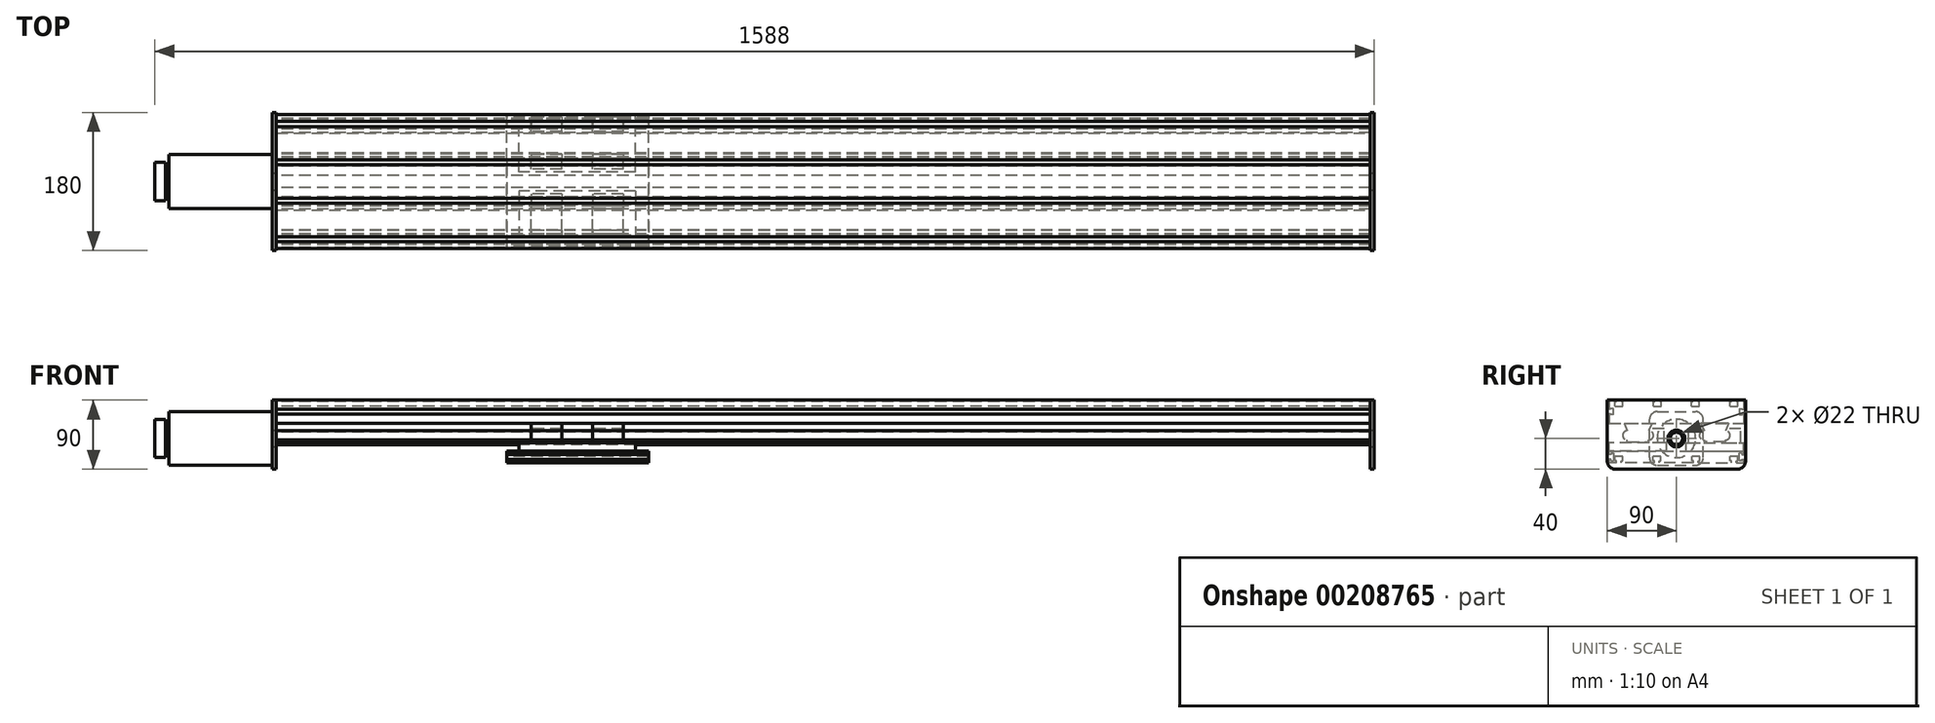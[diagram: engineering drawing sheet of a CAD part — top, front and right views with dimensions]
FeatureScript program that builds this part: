
annotation { "Feature Type Name" : "Feature", "Feature Type Description" : "" }
export const myFeature = defineFeature(function(context is Context, id is Id, definition is map)
    precondition{}
    {
        {
            var Q0;
            Q0=qCreatedBy(makeId("Right.planeOp"),FACE);
            var sketch = newSketch(context, id + "F0", { "sketchPlane" : qUnion([Q0])});
            skLineSegment(sketch, "E0", {"start": v(0, 0) * mm, "end": v(87.5, 0) * mm});
            skLineSegment(sketch, "E1", {"start": v(87.5, 0) * mm, "end": v(87.5, -30) * mm});
            skLineSegment(sketch, "E2.MirrorCS", {"start": v(0, 0) * mm, "end": v(-87.5, 0) * mm});
            skLineSegment(sketch, "E3.MirrorCS", {"start": v(-87.5, 0) * mm, "end": v(-87.5, -30) * mm});
            skLineSegment(sketch, "E4", {"start": v(87.5, 0) * mm, "end": v(78.2, 0) * mm});
            skLineSegment(sketch, "E5", {"start": v(78.2, 0) * mm, "end": v(78.2, -2) * mm});
            skLineSegment(sketch, "E6", {"start": v(78.2, 0) * mm, "end": v(71.75, 0) * mm});
            skLineSegment(sketch, "E7", {"start": v(71.75, 0) * mm, "end": v(71.75, -2) * mm});
            skLineSegment(sketch, "E8", {"start": v(74.98, -8) * mm, "end": v(79.98, -8) * mm});
            skLineSegment(sketch, "E9", {"start": v(74.98, -8) * mm, "end": v(69.98, -8) * mm});
            skLineSegment(sketch, "E10", {"start": v(69.98, -8) * mm, "end": v(69.98, -2) * mm});
            skLineSegment(sketch, "E11", {"start": v(69.98, -2) * mm, "end": v(71.75, -2) * mm});
            skLineSegment(sketch, "E12", {"start": v(74.98, 0) * mm, "end": v(74.98, -8) * mm, "construction": true});
            skLineSegment(sketch, "E13.MirrorCS", {"start": v(79.98, -8) * mm, "end": v(79.98, -2) * mm});
            skLineSegment(sketch, "E14.MirrorCS", {"start": v(79.98, -2) * mm, "end": v(78.2, -2) * mm});
            skLineSegment(sketch, "E15", {"start": v(87.5, 0) * mm, "end": v(28.2, 0) * mm});
            skLineSegment(sketch, "E16", {"start": v(28.2, 0) * mm, "end": v(28.2, -2) * mm});
            skLineSegment(sketch, "E17", {"start": v(28.2, 0) * mm, "end": v(21.75, 0) * mm});
            skLineSegment(sketch, "E18", {"start": v(24.98, 0) * mm, "end": v(24.98, -8) * mm, "construction": true});
            skLineSegment(sketch, "E19", {"start": v(24.98, -8) * mm, "end": v(29.98, -8) * mm});
            skLineSegment(sketch, "E20", {"start": v(24.98, -8) * mm, "end": v(19.98, -8) * mm});
            skLineSegment(sketch, "E21", {"start": v(29.98, -8) * mm, "end": v(29.98, -2) * mm});
            skLineSegment(sketch, "E22", {"start": v(29.98, -2) * mm, "end": v(28.2, -2) * mm});
            skLineSegment(sketch, "E23.MirrorCS", {"start": v(19.98, -8) * mm, "end": v(19.98, -2) * mm});
            skLineSegment(sketch, "E24.MirrorCS", {"start": v(19.98, -2) * mm, "end": v(21.75, -2) * mm});
            skLineSegment(sketch, "E25.MirrorCS", {"start": v(21.75, 0) * mm, "end": v(21.75, -2) * mm});
            skLineSegment(sketch, "E26", {"start": v(87.5, -30) * mm, "end": v(0, -30) * mm});
            skLineSegment(sketch, "E27.MirrorCS", {"start": v(-87.5, -30) * mm, "end": v(0, -30) * mm});
            skLineSegment(sketch, "E28", {"start": v(87.5, -15) * mm, "end": v(82, -15) * mm, "construction": true});
            skLineSegment(sketch, "E29", {"start": v(82, -15) * mm, "end": v(82, -11) * mm});
            skLineSegment(sketch, "E30", {"start": v(82, -15) * mm, "end": v(82, -19) * mm});
            skLineSegment(sketch, "E31", {"start": v(82, -11) * mm, "end": v(86, -11) * mm});
            skLineSegment(sketch, "E32", {"start": v(86, -11) * mm, "end": v(86, -12) * mm});
            skLineSegment(sketch, "E33", {"start": v(86, -12) * mm, "end": v(87.5, -12) * mm});
            skLineSegment(sketch, "E34.MirrorCS", {"start": v(82, -19) * mm, "end": v(86, -19) * mm});
            skLineSegment(sketch, "E35.MirrorCS", {"start": v(86, -19) * mm, "end": v(86, -18) * mm});
            skLineSegment(sketch, "E36.MirrorCS", {"start": v(86, -18) * mm, "end": v(87.5, -18) * mm});
            skLineSegment(sketch, "E37", {"start": v(87.5, -30) * mm, "end": v(68, -30) * mm});
            skLineSegment(sketch, "E38", {"start": v(87.5, -30) * mm, "end": v(87.5, -40) * mm, "construction": true});
            skLineSegment(sketch, "E39", {"start": v(87.5, -40) * mm, "end": v(64, -40) * mm, "construction": true});
            skLineSegment(sketch, "E40", {"start": v(68, -30) * mm, "end": v(64, -40) * mm});
            skLineSegment(sketch, "E41", {"start": v(0, 0) * mm, "end": v(0, -54.5) * mm, "construction": true});
            skLineSegment(sketch, "E42", {"start": v(0, -54.5) * mm, "end": v(87.5, -54.5) * mm, "construction": true});
            skLineSegment(sketch, "E43", {"start": v(64, -54.5) * mm, "end": v(64, -52) * mm});
            skLineSegment(sketch, "E44", {"start": v(64, -40) * mm, "end": v(64, -52) * mm, "construction": true});
            skArc(sketch, "E45", {"start": v(64, -52) * mm, "mid": v(70, -46) * mm, "end": v(64, -40) * mm});
            skLineSegment(sketch, "E46", {"start": v(64, -54.5) * mm, "end": v(36, -54.5) * mm});
            skLineSegment(sketch, "E47", {"start": v(50, -54.5) * mm, "end": v(50, -30) * mm, "construction": true});
            skLineSegment(sketch, "E48.MirrorCS", {"start": v(36, -54.5) * mm, "end": v(36, -52) * mm});
            skArc(sketch, "E49.MirrorCS", {"start": v(36, -52) * mm, "mid": v(30, -46) * mm, "end": v(36, -40) * mm});
            skLineSegment(sketch, "E50.MirrorCS", {"start": v(32, -30) * mm, "end": v(36, -40) * mm});
            skLineSegment(sketch, "E51.MirrorCS", {"start": v(-21.75, 0) * mm, "end": v(-21.75, -2) * mm});
            skLineSegment(sketch, "E52.MirrorCS", {"start": v(-19.98, -2) * mm, "end": v(-21.75, -2) * mm});
            skLineSegment(sketch, "E53.MirrorCS", {"start": v(-19.98, -8) * mm, "end": v(-19.98, -2) * mm});
            skLineSegment(sketch, "E54.MirrorCS", {"start": v(-24.98, -8) * mm, "end": v(-19.98, -8) * mm});
            skLineSegment(sketch, "E55.MirrorCS", {"start": v(-24.98, -8) * mm, "end": v(-29.98, -8) * mm});
            skLineSegment(sketch, "E56.MirrorCS", {"start": v(-29.98, -8) * mm, "end": v(-29.98, -2) * mm});
            skLineSegment(sketch, "E57.MirrorCS", {"start": v(-29.98, -2) * mm, "end": v(-28.2, -2) * mm});
            skLineSegment(sketch, "E58.MirrorCS", {"start": v(-28.2, 0) * mm, "end": v(-28.2, -2) * mm});
            skLineSegment(sketch, "E59.MirrorCS", {"start": v(-71.75, 0) * mm, "end": v(-71.75, -2) * mm});
            skLineSegment(sketch, "E60.MirrorCS", {"start": v(-69.98, -2) * mm, "end": v(-71.75, -2) * mm});
            skLineSegment(sketch, "E61.MirrorCS", {"start": v(-69.98, -8) * mm, "end": v(-69.98, -2) * mm});
            skLineSegment(sketch, "E62.MirrorCS", {"start": v(-74.98, -8) * mm, "end": v(-69.98, -8) * mm});
            skLineSegment(sketch, "E63.MirrorCS", {"start": v(-74.98, -8) * mm, "end": v(-79.98, -8) * mm});
            skLineSegment(sketch, "E64.MirrorCS", {"start": v(-79.98, -8) * mm, "end": v(-79.98, -2) * mm});
            skLineSegment(sketch, "E65.MirrorCS", {"start": v(-79.98, -2) * mm, "end": v(-78.2, -2) * mm});
            skLineSegment(sketch, "E66.MirrorCS", {"start": v(-78.2, 0) * mm, "end": v(-78.2, -2) * mm});
            skLineSegment(sketch, "E67.MirrorCS", {"start": v(-86, -12) * mm, "end": v(-87.5, -12) * mm});
            skLineSegment(sketch, "E68.MirrorCS", {"start": v(-86, -11) * mm, "end": v(-86, -12) * mm});
            skLineSegment(sketch, "E69.MirrorCS", {"start": v(-82, -11) * mm, "end": v(-86, -11) * mm});
            skLineSegment(sketch, "E70.MirrorCS", {"start": v(-82, -15) * mm, "end": v(-82, -11) * mm});
            skLineSegment(sketch, "E71.MirrorCS", {"start": v(-82, -15) * mm, "end": v(-82, -19) * mm});
            skLineSegment(sketch, "E72.MirrorCS", {"start": v(-82, -19) * mm, "end": v(-86, -19) * mm});
            skLineSegment(sketch, "E73.MirrorCS", {"start": v(-86, -19) * mm, "end": v(-86, -18) * mm});
            skLineSegment(sketch, "E74.MirrorCS", {"start": v(-86, -18) * mm, "end": v(-87.5, -18) * mm});
            skLineSegment(sketch, "E75.MirrorCS", {"start": v(-68, -30) * mm, "end": v(-64, -40) * mm});
            skArc(sketch, "E76.MirrorCS", {"start": v(-64, -52) * mm, "mid": v(-70, -46) * mm, "end": v(-64, -40) * mm});
            skLineSegment(sketch, "E77.MirrorCS", {"start": v(-64, -54.5) * mm, "end": v(-64, -52) * mm});
            skLineSegment(sketch, "E78.MirrorCS", {"start": v(-36, -54.5) * mm, "end": v(-36, -52) * mm});
            skArc(sketch, "E79.MirrorCS", {"start": v(-36, -52) * mm, "mid": v(-30, -46) * mm, "end": v(-36, -40) * mm});
            skLineSegment(sketch, "E80.MirrorCS", {"start": v(-32, -30) * mm, "end": v(-36, -40) * mm});
            skLineSegment(sketch, "E81", {"start": v(-64, -54.5) * mm, "end": v(-36, -54.5) * mm});
            skLineSegment(sketch, "E82", {"start": v(0, -54.5) * mm, "end": v(0, -55.5) * mm, "construction": true});
            skLineSegment(sketch, "E83", {"start": v(87.5, -54.5) * mm, "end": v(87.5, -55.5) * mm, "construction": true});
            skLineSegment(sketch, "E84", {"start": v(0, -81.5) * mm, "end": v(87.5, -81.5) * mm});
            skLineSegment(sketch, "E85", {"start": v(87.5, -81.5) * mm, "end": v(87.5, -55.5) * mm});
            skLineSegment(sketch, "E86", {"start": v(0, -55.5) * mm, "end": v(0, -81.5) * mm, "construction": true});
            skLineSegment(sketch, "E87", {"start": v(0, -55.5) * mm, "end": v(12.5, -55.5) * mm, "construction": true});
            skLineSegment(sketch, "E88", {"start": v(12.5, -66.5) * mm, "end": v(12.5, -55.5) * mm});
            skLineSegment(sketch, "E89", {"start": v(12.5, -66.5) * mm, "end": v(0, -66.5) * mm});
            skLineSegment(sketch, "E90", {"start": v(0, -66.5) * mm, "end": v(0, -81.5) * mm});
            skLineSegment(sketch, "E91.MirrorCS", {"start": v(0, -81.5) * mm, "end": v(-87.5, -81.5) * mm});
            skLineSegment(sketch, "E92.MirrorCS", {"start": v(-87.5, -81.5) * mm, "end": v(-87.5, -55.5) * mm});
            skLineSegment(sketch, "E93.MirrorCS", {"start": v(-12.5, -66.5) * mm, "end": v(0, -66.5) * mm});
            skLineSegment(sketch, "E94.MirrorCS", {"start": v(-12.5, -66.5) * mm, "end": v(-12.5, -55.5) * mm});
            skLineSegment(sketch, "E95", {"start": v(12.5, -55.5) * mm, "end": v(87.5, -55.5) * mm});
            skLineSegment(sketch, "E96.MirrorCS", {"start": v(-12.5, -55.5) * mm, "end": v(-87.5, -55.5) * mm});
            skLineSegment(sketch, "E97", {"start": v(-12.5, -66.5) * mm, "end": v(-87.5, -66.5) * mm});
            skLineSegment(sketch, "E98", {"start": v(12.5, -66.5) * mm, "end": v(87.5, -66.5) * mm});
            skLineSegment(sketch, "E99", {"start": v(-87.5, -55.5) * mm, "end": v(-84, -55.5) * mm, "construction": true});
            skLineSegment(sketch, "E100", {"start": v(-84, -55.5) * mm, "end": v(-84, -37.5) * mm});
            skLineSegment(sketch, "E101", {"start": v(-84, -37.5) * mm, "end": v(-65, -37.5) * mm});
            skLineSegment(sketch, "E102", {"start": v(-64, -54.5) * mm, "end": v(-64, -55.5) * mm});
            skLineSegment(sketch, "E103.MirrorCS", {"start": v(84, -37.5) * mm, "end": v(65, -37.5) * mm});
            skLineSegment(sketch, "E104.MirrorCS", {"start": v(84, -55.5) * mm, "end": v(84, -37.5) * mm});
            skLineSegment(sketch, "E105.MirrorCS", {"start": v(64, -54.5) * mm, "end": v(64, -55.5) * mm});
            skLineSegment(sketch, "E106", {"start": v(-50, -54.5) * mm, "end": v(-50, -30) * mm, "construction": true});
            skLineSegment(sketch, "E107.MirrorCS", {"start": v(-16, -37.5) * mm, "end": v(-35, -37.5) * mm});
            skLineSegment(sketch, "E108.MirrorCS", {"start": v(-16, -55.5) * mm, "end": v(-16, -37.5) * mm});
            skLineSegment(sketch, "E109.MirrorCS", {"start": v(-36, -54.5) * mm, "end": v(-36, -55.5) * mm});
            skLineSegment(sketch, "E110.MirrorCS", {"start": v(16, -37.5) * mm, "end": v(35, -37.5) * mm});
            skLineSegment(sketch, "E111.MirrorCS", {"start": v(16, -55.5) * mm, "end": v(16, -37.5) * mm});
            skLineSegment(sketch, "E112.MirrorCS", {"start": v(36, -54.5) * mm, "end": v(36, -55.5) * mm});
            skLineSegment(sketch, "E113", {"start": v(-87.5, -81.5) * mm, "end": v(-78.3, -81.5) * mm});
            skLineSegment(sketch, "E114", {"start": v(-78.3, -81.5) * mm, "end": v(-71.85, -81.5) * mm});
            skLineSegment(sketch, "E115", {"start": v(-71.85, -81.5) * mm, "end": v(-28.45, -81.5) * mm});
            skLineSegment(sketch, "E116", {"start": v(-28.45, -81.5) * mm, "end": v(-22, -81.5) * mm});
            skLineSegment(sketch, "E117", {"start": v(-22, -81.5) * mm, "end": v(0, -81.5) * mm});
            skLineSegment(sketch, "E118", {"start": v(-78.3, -81.5) * mm, "end": v(-78.3, -79) * mm});
            skLineSegment(sketch, "E119", {"start": v(-75.08, -81.5) * mm, "end": v(-75.08, -73.5) * mm, "construction": true});
            skLineSegment(sketch, "E120", {"start": v(-75.08, -73.5) * mm, "end": v(-80.08, -73.5) * mm});
            skLineSegment(sketch, "E121", {"start": v(-75.08, -73.5) * mm, "end": v(-70.08, -73.5) * mm});
            skLineSegment(sketch, "E122", {"start": v(-78.3, -79) * mm, "end": v(-80.08, -79) * mm});
            skLineSegment(sketch, "E123", {"start": v(-80.08, -79) * mm, "end": v(-80.08, -73.5) * mm});
            skLineSegment(sketch, "E124.MirrorCS", {"start": v(-70.08, -79) * mm, "end": v(-70.08, -73.5) * mm});
            skLineSegment(sketch, "E125.MirrorCS", {"start": v(-71.85, -79) * mm, "end": v(-70.08, -79) * mm});
            skLineSegment(sketch, "E126.MirrorCS", {"start": v(-71.85, -81.5) * mm, "end": v(-71.85, -79) * mm});
            skLineSegment(sketch, "E127", {"start": v(-50.15, -81.5) * mm, "end": v(-50.15, -66.5) * mm, "construction": true});
            skLineSegment(sketch, "E128.MirrorCS", {"start": v(-28.45, -81.5) * mm, "end": v(-28.45, -79) * mm});
            skLineSegment(sketch, "E129.MirrorCS", {"start": v(-28.45, -79) * mm, "end": v(-30.23, -79) * mm});
            skLineSegment(sketch, "E130.MirrorCS", {"start": v(-30.23, -79) * mm, "end": v(-30.23, -73.5) * mm});
            skLineSegment(sketch, "E131.MirrorCS", {"start": v(-25.22, -73.5) * mm, "end": v(-30.23, -73.5) * mm});
            skLineSegment(sketch, "E132.MirrorCS", {"start": v(-25.22, -73.5) * mm, "end": v(-20.22, -73.5) * mm});
            skLineSegment(sketch, "E133.MirrorCS", {"start": v(-20.22, -79) * mm, "end": v(-20.22, -73.5) * mm});
            skLineSegment(sketch, "E134.MirrorCS", {"start": v(-22, -79) * mm, "end": v(-20.22, -79) * mm});
            skLineSegment(sketch, "E135.MirrorCS", {"start": v(-22, -81.5) * mm, "end": v(-22, -79) * mm});
            skLineSegment(sketch, "E136.MirrorCS", {"start": v(22, -81.5) * mm, "end": v(22, -79) * mm});
            skLineSegment(sketch, "E137.MirrorCS", {"start": v(22, -79) * mm, "end": v(20.23, -79) * mm});
            skLineSegment(sketch, "E138.MirrorCS", {"start": v(20.23, -79) * mm, "end": v(20.23, -73.5) * mm});
            skLineSegment(sketch, "E139.MirrorCS", {"start": v(25.23, -73.5) * mm, "end": v(20.23, -73.5) * mm});
            skLineSegment(sketch, "E140.MirrorCS", {"start": v(25.23, -73.5) * mm, "end": v(30.23, -73.5) * mm});
            skLineSegment(sketch, "E141.MirrorCS", {"start": v(30.23, -79) * mm, "end": v(30.23, -73.5) * mm});
            skLineSegment(sketch, "E142.MirrorCS", {"start": v(28.45, -79) * mm, "end": v(30.23, -79) * mm});
            skLineSegment(sketch, "E143.MirrorCS", {"start": v(28.45, -81.5) * mm, "end": v(28.45, -79) * mm});
            skLineSegment(sketch, "E144.MirrorCS", {"start": v(71.85, -81.5) * mm, "end": v(71.85, -79) * mm});
            skLineSegment(sketch, "E145.MirrorCS", {"start": v(71.85, -79) * mm, "end": v(70.08, -79) * mm});
            skLineSegment(sketch, "E146.MirrorCS", {"start": v(70.08, -79) * mm, "end": v(70.08, -73.5) * mm});
            skLineSegment(sketch, "E147.MirrorCS", {"start": v(75.08, -73.5) * mm, "end": v(70.08, -73.5) * mm});
            skLineSegment(sketch, "E148.MirrorCS", {"start": v(75.08, -73.5) * mm, "end": v(80.08, -73.5) * mm});
            skLineSegment(sketch, "E149.MirrorCS", {"start": v(80.08, -79) * mm, "end": v(80.08, -73.5) * mm});
            skLineSegment(sketch, "E150.MirrorCS", {"start": v(78.3, -79) * mm, "end": v(80.08, -79) * mm});
            skLineSegment(sketch, "E151.MirrorCS", {"start": v(78.3, -81.5) * mm, "end": v(78.3, -79) * mm});
            skLineSegment(sketch, "E152", {"start": v(-82.08, -69) * mm, "end": v(-82.08, -79) * mm});
            skLineSegment(sketch, "E153", {"start": v(-87.5, -79) * mm, "end": v(-85, -79) * mm, "construction": true});
            skLineSegment(sketch, "E154", {"start": v(-85, -79) * mm, "end": v(-82.08, -79) * mm});
            skLineSegment(sketch, "E155", {"start": v(-85, -79) * mm, "end": v(-85, -77) * mm});
            skLineSegment(sketch, "E156", {"start": v(-85, -77) * mm, "end": v(-87.5, -77) * mm});
            skLineSegment(sketch, "E157", {"start": v(-82.08, -74) * mm, "end": v(-87.5, -74) * mm, "construction": true});
            skLineSegment(sketch, "E158.MirrorCS", {"start": v(-85, -71) * mm, "end": v(-87.5, -71) * mm});
            skLineSegment(sketch, "E159.MirrorCS", {"start": v(-85, -69) * mm, "end": v(-85, -71) * mm});
            skLineSegment(sketch, "E160.MirrorCS", {"start": v(-85, -69) * mm, "end": v(-82.08, -69) * mm});
            skLineSegment(sketch, "E161.MirrorCS", {"start": v(-82.08, -79) * mm, "end": v(-82.08, -69) * mm});
            skLineSegment(sketch, "E162", {"start": v(-87.5, -66.5) * mm, "end": v(-87.5, -74) * mm, "construction": true});
            skLineSegment(sketch, "E163.MirrorCS", {"start": v(85, -77) * mm, "end": v(87.5, -77) * mm});
            skLineSegment(sketch, "E164.MirrorCS", {"start": v(85, -79) * mm, "end": v(85, -77) * mm});
            skLineSegment(sketch, "E165.MirrorCS", {"start": v(85, -79) * mm, "end": v(82.08, -79) * mm});
            skLineSegment(sketch, "E166.MirrorCS", {"start": v(82.08, -79) * mm, "end": v(82.08, -69) * mm});
            skLineSegment(sketch, "E167.MirrorCS", {"start": v(85, -69) * mm, "end": v(82.08, -69) * mm});
            skLineSegment(sketch, "E168.MirrorCS", {"start": v(85, -69) * mm, "end": v(85, -71) * mm});
            skLineSegment(sketch, "E169.MirrorCS", {"start": v(85, -71) * mm, "end": v(87.5, -71) * mm});
            skSolve(sketch);
        }
        {
            var Q0;
            {var subQ22=sQuery(id+"F0.wireOp",EDGE,"E0");Q0=makeQuery(id+"F0.imprint","IMPRINT",FACE,{"disambiguationData":[TD([[makeQuery(id+"F0.imprint","IMPRINT",EDGE,{"derivedFrom":subQ22}),-1.0]])]});}
            extrude(context, id + "F1", {"entities" : qUnion([Q0]), "depth" : 1425 * mm});
        }
        {
            var Q0;
            {var subQ0=sQuery(id+"F0.wireOp",EDGE,"E40");Q0=makeQuery(id+"F0.imprint","IMPRINT",FACE,{"disambiguationData":[TD([[makeQuery(id+"F0.imprint","IMPRINT",EDGE,{"derivedFrom":subQ0}),-1.0]])]});}
            var Q1;
            {var subQ0=sQuery(id+"F0.wireOp",EDGE,"E75.MirrorCS");Q1=makeQuery(id+"F0.imprint","IMPRINT",FACE,{"disambiguationData":[TD([[makeQuery(id+"F0.imprint","IMPRINT",EDGE,{"derivedFrom":subQ0}),1.0]])]});}
            extrude(context, id + "F2", {"entities" : qUnion([Q0, Q1]), "depth" : 1425 * mm});
        }
        {
            var Q0;
            Q0=makeQuery(id+"F2.opExtrude","SWEPT_EDGE",EDGE,{"disambiguationData":[OSD([sQuery(id+"F0.wireOp",EDGE,"E77.MirrorCS"),sQuery(id+"F0.wireOp",EDGE,"E81")])]});
            var Q1;
            Q1=makeQuery(id+"F2.opExtrude","SWEPT_EDGE",EDGE,{"disambiguationData":[OSD([sQuery(id+"F0.wireOp",EDGE,"E78.MirrorCS"),sQuery(id+"F0.wireOp",EDGE,"E81")])]});
            var Q2;
            Q2=makeQuery(id+"F2.opExtrude","SWEPT_EDGE",EDGE,{"disambiguationData":[OSD([sQuery(id+"F0.wireOp",EDGE,"E46"),sQuery(id+"F0.wireOp",EDGE,"E48.MirrorCS")])]});
            var Q3;
            Q3=makeQuery(id+"F2.opExtrude","SWEPT_EDGE",EDGE,{"disambiguationData":[OSD([sQuery(id+"F0.wireOp",EDGE,"E43"),sQuery(id+"F0.wireOp",EDGE,"E46")])]});
            chamfer(context, id + "F3", {"entities" : qUnion([Q0, Q1, Q2, Q3]), "width" : 1 * mm, "tangentPropagation" : true});
        }
        {
            var Q0;
            Q0=makeQuery(id+"F0.imprint","IMPRINT",FACE,{"disambiguationData":[TD([[makeQuery(id+"F0.imprint","IMPRINT",EDGE,{"derivedFrom":sQuery(id+"F0.wireOp",EDGE,"E94.MirrorCS")}),1.0]])]});
            var Q1;
            Q1=makeQuery(id+"F0.imprint","IMPRINT",FACE,{"disambiguationData":[TD([[makeQuery(id+"F0.imprint","IMPRINT",EDGE,{"derivedFrom":sQuery(id+"F0.wireOp",EDGE,"E88")}),-1.0]])]});
            extrude(context, id + "F4", {"entities" : qUnion([Q0, Q1]), "depth" : 152 * mm});
        }
        {
            var Q0;
            Q0=makeQuery(id+"F0.imprint","IMPRINT",FACE,{"disambiguationData":[TD([[makeQuery(id+"F0.imprint","IMPRINT",EDGE,{"derivedFrom":sQuery(id+"F0.wireOp",EDGE,"E90")}),-1.0]])]});
            var Q1;
            {var subQ1=sQuery(id+"F0.wireOp",EDGE,"E84");Q1=makeQuery(id+"F0.imprint","IMPRINT",FACE,{"disambiguationData":[TD([[makeQuery(id+"F0.imprint","IMPRINT",EDGE,{"derivedFrom":subQ1}),1.0]])]});}
            extrude(context, id + "F5", {"entities" : qUnion([Q0, Q1]), "depth" : 185 * mm});
        }
        {
            var Q0;
            {var subQ4=sQuery(id+"F0.wireOp",EDGE,"E76.MirrorCS");Q0=makeQuery(id+"F0.imprint","IMPRINT",FACE,{"disambiguationData":[TD([[makeQuery(id+"F0.imprint","IMPRINT",EDGE,{"derivedFrom":subQ4}),1.0]])]});}
            var Q1;
            Q1=makeQuery(id+"F0.imprint","IMPRINT",FACE,{"disambiguationData":[TD([[makeQuery(id+"F0.imprint","IMPRINT",EDGE,{"derivedFrom":sQuery(id+"F0.wireOp",EDGE,"E43")}),-1.0]])]});
            var Q2;
            Q2=makeQuery(id+"F0.imprint","IMPRINT",FACE,{"disambiguationData":[TD([[makeQuery(id+"F0.imprint","IMPRINT",EDGE,{"derivedFrom":sQuery(id+"F0.wireOp",EDGE,"E78.MirrorCS")}),-1.0]])]});
            var Q3;
            Q3=makeQuery(id+"F0.imprint","IMPRINT",FACE,{"disambiguationData":[TD([[makeQuery(id+"F0.imprint","IMPRINT",EDGE,{"derivedFrom":sQuery(id+"F0.wireOp",EDGE,"E48.MirrorCS")}),1.0]])]});
            extrude(context, id + "F6", {"entities" : qUnion([Q0, Q1, Q2, Q3]), "depth" : 40 * mm});
        }
        {
            var Q0;
            Q0=makeQuery(id+"F4.opExtrude","SWEPT_BODY",BODY,{"disambiguationData":[OSD([sQuery(id+"F0.wireOp",EDGE,"E85"),sQuery(id+"F0.wireOp",EDGE,"E88"),sQuery(id+"F0.wireOp",EDGE,"E95"),sQuery(id+"F0.wireOp",EDGE,"E98")])]});
            var Q1;
            Q1=makeQuery(id+"F4.opExtrude","SWEPT_BODY",BODY,{"disambiguationData":[OSD([sQuery(id+"F0.wireOp",EDGE,"E92.MirrorCS"),sQuery(id+"F0.wireOp",EDGE,"E94.MirrorCS"),sQuery(id+"F0.wireOp",EDGE,"E96.MirrorCS"),sQuery(id+"F0.wireOp",EDGE,"E97")])]});
            transform(context, id + "F7", {"entities" : qUnion([Q0, Q1]), "transformType" : TransformType.TRANSLATION_3D, "dx" : 16 * mm, "dy" : 0 * mm, "dz" : 0 * mm, "makeCopy" : false});
        }
        {
            var Q0;
            Q0=makeQuery(id+"F6.opExtrude","SWEPT_BODY",BODY,{"disambiguationData":[OSD([sQuery(id+"F0.wireOp",EDGE,"E75.MirrorCS"),sQuery(id+"F0.wireOp",EDGE,"E76.MirrorCS"),sQuery(id+"F0.wireOp",EDGE,"E77.MirrorCS"),sQuery(id+"F0.wireOp",EDGE,"E96.MirrorCS"),sQuery(id+"F0.wireOp",EDGE,"E100"),sQuery(id+"F0.wireOp",EDGE,"E101"),sQuery(id+"F0.wireOp",EDGE,"E102")])]});
            var Q1;
            Q1=makeQuery(id+"F6.opExtrude","SWEPT_BODY",BODY,{"disambiguationData":[OSD([sQuery(id+"F0.wireOp",EDGE,"E78.MirrorCS"),sQuery(id+"F0.wireOp",EDGE,"E79.MirrorCS"),sQuery(id+"F0.wireOp",EDGE,"E80.MirrorCS"),sQuery(id+"F0.wireOp",EDGE,"E96.MirrorCS"),sQuery(id+"F0.wireOp",EDGE,"E107.MirrorCS"),sQuery(id+"F0.wireOp",EDGE,"E108.MirrorCS"),sQuery(id+"F0.wireOp",EDGE,"E109.MirrorCS")])]});
            var Q2;
            Q2=makeQuery(id+"F6.opExtrude","SWEPT_BODY",BODY,{"disambiguationData":[OSD([sQuery(id+"F0.wireOp",EDGE,"E48.MirrorCS"),sQuery(id+"F0.wireOp",EDGE,"E49.MirrorCS"),sQuery(id+"F0.wireOp",EDGE,"E50.MirrorCS"),sQuery(id+"F0.wireOp",EDGE,"E95"),sQuery(id+"F0.wireOp",EDGE,"E110.MirrorCS"),sQuery(id+"F0.wireOp",EDGE,"E111.MirrorCS"),sQuery(id+"F0.wireOp",EDGE,"E112.MirrorCS")])]});
            var Q3;
            Q3=makeQuery(id+"F6.opExtrude","SWEPT_BODY",BODY,{"disambiguationData":[OSD([sQuery(id+"F0.wireOp",EDGE,"E40"),sQuery(id+"F0.wireOp",EDGE,"E43"),sQuery(id+"F0.wireOp",EDGE,"E45"),sQuery(id+"F0.wireOp",EDGE,"E95"),sQuery(id+"F0.wireOp",EDGE,"E103.MirrorCS"),sQuery(id+"F0.wireOp",EDGE,"E104.MirrorCS"),sQuery(id+"F0.wireOp",EDGE,"E105.MirrorCS")])]});
            transform(context, id + "F8", {"entities" : qUnion([Q0, Q1, Q2, Q3]), "transformType" : TransformType.TRANSLATION_3D, "dx" : 32 * mm, "dy" : 0 * mm, "dz" : 0 * mm, "makeCopy" : false});
        }
        {
            var Q0;
            Q0=makeQuery(id+"F6.opExtrude","SWEPT_BODY",BODY,{"disambiguationData":[OSD([sQuery(id+"F0.wireOp",EDGE,"E75.MirrorCS"),sQuery(id+"F0.wireOp",EDGE,"E76.MirrorCS"),sQuery(id+"F0.wireOp",EDGE,"E77.MirrorCS"),sQuery(id+"F0.wireOp",EDGE,"E96.MirrorCS"),sQuery(id+"F0.wireOp",EDGE,"E100"),sQuery(id+"F0.wireOp",EDGE,"E101"),sQuery(id+"F0.wireOp",EDGE,"E102")])]});
            var Q1;
            Q1=makeQuery(id+"F6.opExtrude","SWEPT_BODY",BODY,{"disambiguationData":[OSD([sQuery(id+"F0.wireOp",EDGE,"E78.MirrorCS"),sQuery(id+"F0.wireOp",EDGE,"E79.MirrorCS"),sQuery(id+"F0.wireOp",EDGE,"E80.MirrorCS"),sQuery(id+"F0.wireOp",EDGE,"E96.MirrorCS"),sQuery(id+"F0.wireOp",EDGE,"E107.MirrorCS"),sQuery(id+"F0.wireOp",EDGE,"E108.MirrorCS"),sQuery(id+"F0.wireOp",EDGE,"E109.MirrorCS")])]});
            var Q2;
            Q2=makeQuery(id+"F6.opExtrude","SWEPT_BODY",BODY,{"disambiguationData":[OSD([sQuery(id+"F0.wireOp",EDGE,"E48.MirrorCS"),sQuery(id+"F0.wireOp",EDGE,"E49.MirrorCS"),sQuery(id+"F0.wireOp",EDGE,"E50.MirrorCS"),sQuery(id+"F0.wireOp",EDGE,"E95"),sQuery(id+"F0.wireOp",EDGE,"E110.MirrorCS"),sQuery(id+"F0.wireOp",EDGE,"E111.MirrorCS"),sQuery(id+"F0.wireOp",EDGE,"E112.MirrorCS")])]});
            var Q3;
            Q3=makeQuery(id+"F6.opExtrude","SWEPT_BODY",BODY,{"disambiguationData":[OSD([sQuery(id+"F0.wireOp",EDGE,"E40"),sQuery(id+"F0.wireOp",EDGE,"E43"),sQuery(id+"F0.wireOp",EDGE,"E45"),sQuery(id+"F0.wireOp",EDGE,"E95"),sQuery(id+"F0.wireOp",EDGE,"E103.MirrorCS"),sQuery(id+"F0.wireOp",EDGE,"E104.MirrorCS"),sQuery(id+"F0.wireOp",EDGE,"E105.MirrorCS")])]});
            transform(context, id + "F9", {"entities" : qUnion([Q0, Q1, Q2, Q3]), "transformType" : TransformType.TRANSLATION_3D, "dx" : 80 * mm, "dy" : 0 * mm, "dz" : 0 * mm, "makeCopy" : true});
        }
        {
            var Q0;
            Q0=makeQuery(id+"F5.opExtrude","SWEPT_BODY",BODY,{"disambiguationData":[OSD([sQuery(id+"F0.wireOp",EDGE,"E84"),sQuery(id+"F0.wireOp",EDGE,"E85"),sQuery(id+"F0.wireOp",EDGE,"E89"),sQuery(id+"F0.wireOp",EDGE,"E92.MirrorCS"),sQuery(id+"F0.wireOp",EDGE,"E93.MirrorCS"),sQuery(id+"F0.wireOp",EDGE,"E97"),sQuery(id+"F0.wireOp",EDGE,"E98"),sQuery(id+"F0.wireOp",EDGE,"E113"),sQuery(id+"F0.wireOp",EDGE,"E115"),sQuery(id+"F0.wireOp",EDGE,"E117"),sQuery(id+"F0.wireOp",EDGE,"E118"),sQuery(id+"F0.wireOp",EDGE,"E120"),sQuery(id+"F0.wireOp",EDGE,"E121"),sQuery(id+"F0.wireOp",EDGE,"E122"),sQuery(id+"F0.wireOp",EDGE,"E123"),sQuery(id+"F0.wireOp",EDGE,"E124.MirrorCS"),sQuery(id+"F0.wireOp",EDGE,"E125.MirrorCS"),sQuery(id+"F0.wireOp",EDGE,"E126.MirrorCS"),sQuery(id+"F0.wireOp",EDGE,"E128.MirrorCS"),sQuery(id+"F0.wireOp",EDGE,"E129.MirrorCS"),sQuery(id+"F0.wireOp",EDGE,"E130.MirrorCS"),sQuery(id+"F0.wireOp",EDGE,"E131.MirrorCS"),sQuery(id+"F0.wireOp",EDGE,"E132.MirrorCS"),sQuery(id+"F0.wireOp",EDGE,"E133.MirrorCS"),sQuery(id+"F0.wireOp",EDGE,"E134.MirrorCS"),sQuery(id+"F0.wireOp",EDGE,"E135.MirrorCS"),sQuery(id+"F0.wireOp",EDGE,"E136.MirrorCS"),sQuery(id+"F0.wireOp",EDGE,"E137.MirrorCS"),sQuery(id+"F0.wireOp",EDGE,"E138.MirrorCS"),sQuery(id+"F0.wireOp",EDGE,"E139.MirrorCS"),sQuery(id+"F0.wireOp",EDGE,"E140.MirrorCS"),sQuery(id+"F0.wireOp",EDGE,"E141.MirrorCS"),sQuery(id+"F0.wireOp",EDGE,"E142.MirrorCS"),sQuery(id+"F0.wireOp",EDGE,"E143.MirrorCS"),sQuery(id+"F0.wireOp",EDGE,"E144.MirrorCS"),sQuery(id+"F0.wireOp",EDGE,"E145.MirrorCS"),sQuery(id+"F0.wireOp",EDGE,"E146.MirrorCS"),sQuery(id+"F0.wireOp",EDGE,"E147.MirrorCS"),sQuery(id+"F0.wireOp",EDGE,"E148.MirrorCS"),sQuery(id+"F0.wireOp",EDGE,"E149.MirrorCS"),sQuery(id+"F0.wireOp",EDGE,"E150.MirrorCS"),sQuery(id+"F0.wireOp",EDGE,"E151.MirrorCS"),sQuery(id+"F0.wireOp",EDGE,"E154"),sQuery(id+"F0.wireOp",EDGE,"E155"),sQuery(id+"F0.wireOp",EDGE,"E156"),sQuery(id+"F0.wireOp",EDGE,"E158.MirrorCS"),sQuery(id+"F0.wireOp",EDGE,"E159.MirrorCS"),sQuery(id+"F0.wireOp",EDGE,"E160.MirrorCS"),sQuery(id+"F0.wireOp",EDGE,"E161.MirrorCS"),sQuery(id+"F0.wireOp",EDGE,"E163.MirrorCS"),sQuery(id+"F0.wireOp",EDGE,"E164.MirrorCS"),sQuery(id+"F0.wireOp",EDGE,"E165.MirrorCS"),sQuery(id+"F0.wireOp",EDGE,"E166.MirrorCS"),sQuery(id+"F0.wireOp",EDGE,"E167.MirrorCS"),sQuery(id+"F0.wireOp",EDGE,"E168.MirrorCS"),sQuery(id+"F0.wireOp",EDGE,"E169.MirrorCS")])]});
            var Q1;
            Q1=makeQuery(id+"F4.opExtrude","SWEPT_BODY",BODY,{"disambiguationData":[OSD([sQuery(id+"F0.wireOp",EDGE,"E92.MirrorCS"),sQuery(id+"F0.wireOp",EDGE,"E94.MirrorCS"),sQuery(id+"F0.wireOp",EDGE,"E96.MirrorCS"),sQuery(id+"F0.wireOp",EDGE,"E97")])]});
            var Q2;
            Q2=makeQuery(id+"F4.opExtrude","SWEPT_BODY",BODY,{"disambiguationData":[OSD([sQuery(id+"F0.wireOp",EDGE,"E85"),sQuery(id+"F0.wireOp",EDGE,"E88"),sQuery(id+"F0.wireOp",EDGE,"E95"),sQuery(id+"F0.wireOp",EDGE,"E98")])]});
            var Q3;
            Q3=makeQuery(id+"F9.opPattern","COPY",BODY,{"derivedFrom":makeQuery(id+"F6.opExtrude","SWEPT_BODY",BODY,{"disambiguationData":[OSD([sQuery(id+"F0.wireOp",EDGE,"E75.MirrorCS"),sQuery(id+"F0.wireOp",EDGE,"E76.MirrorCS"),sQuery(id+"F0.wireOp",EDGE,"E77.MirrorCS"),sQuery(id+"F0.wireOp",EDGE,"E96.MirrorCS"),sQuery(id+"F0.wireOp",EDGE,"E100"),sQuery(id+"F0.wireOp",EDGE,"E101"),sQuery(id+"F0.wireOp",EDGE,"E102")])]}),"instanceName":"1"});
            var Q4;
            Q4=makeQuery(id+"F6.opExtrude","SWEPT_BODY",BODY,{"disambiguationData":[OSD([sQuery(id+"F0.wireOp",EDGE,"E75.MirrorCS"),sQuery(id+"F0.wireOp",EDGE,"E76.MirrorCS"),sQuery(id+"F0.wireOp",EDGE,"E77.MirrorCS"),sQuery(id+"F0.wireOp",EDGE,"E96.MirrorCS"),sQuery(id+"F0.wireOp",EDGE,"E100"),sQuery(id+"F0.wireOp",EDGE,"E101"),sQuery(id+"F0.wireOp",EDGE,"E102")])]});
            var Q5;
            Q5=makeQuery(id+"F9.opPattern","COPY",BODY,{"derivedFrom":makeQuery(id+"F6.opExtrude","SWEPT_BODY",BODY,{"disambiguationData":[OSD([sQuery(id+"F0.wireOp",EDGE,"E40"),sQuery(id+"F0.wireOp",EDGE,"E43"),sQuery(id+"F0.wireOp",EDGE,"E45"),sQuery(id+"F0.wireOp",EDGE,"E95"),sQuery(id+"F0.wireOp",EDGE,"E103.MirrorCS"),sQuery(id+"F0.wireOp",EDGE,"E104.MirrorCS"),sQuery(id+"F0.wireOp",EDGE,"E105.MirrorCS")])]}),"instanceName":"1"});
            var Q6;
            Q6=makeQuery(id+"F6.opExtrude","SWEPT_BODY",BODY,{"disambiguationData":[OSD([sQuery(id+"F0.wireOp",EDGE,"E40"),sQuery(id+"F0.wireOp",EDGE,"E43"),sQuery(id+"F0.wireOp",EDGE,"E45"),sQuery(id+"F0.wireOp",EDGE,"E95"),sQuery(id+"F0.wireOp",EDGE,"E103.MirrorCS"),sQuery(id+"F0.wireOp",EDGE,"E104.MirrorCS"),sQuery(id+"F0.wireOp",EDGE,"E105.MirrorCS")])]});
            var Q7;
            Q7=makeQuery(id+"F6.opExtrude","SWEPT_BODY",BODY,{"disambiguationData":[OSD([sQuery(id+"F0.wireOp",EDGE,"E48.MirrorCS"),sQuery(id+"F0.wireOp",EDGE,"E49.MirrorCS"),sQuery(id+"F0.wireOp",EDGE,"E50.MirrorCS"),sQuery(id+"F0.wireOp",EDGE,"E95"),sQuery(id+"F0.wireOp",EDGE,"E110.MirrorCS"),sQuery(id+"F0.wireOp",EDGE,"E111.MirrorCS"),sQuery(id+"F0.wireOp",EDGE,"E112.MirrorCS")])]});
            var Q8;
            Q8=makeQuery(id+"F9.opPattern","COPY",BODY,{"derivedFrom":makeQuery(id+"F6.opExtrude","SWEPT_BODY",BODY,{"disambiguationData":[OSD([sQuery(id+"F0.wireOp",EDGE,"E48.MirrorCS"),sQuery(id+"F0.wireOp",EDGE,"E49.MirrorCS"),sQuery(id+"F0.wireOp",EDGE,"E50.MirrorCS"),sQuery(id+"F0.wireOp",EDGE,"E95"),sQuery(id+"F0.wireOp",EDGE,"E110.MirrorCS"),sQuery(id+"F0.wireOp",EDGE,"E111.MirrorCS"),sQuery(id+"F0.wireOp",EDGE,"E112.MirrorCS")])]}),"instanceName":"1"});
            var Q9;
            Q9=makeQuery(id+"F6.opExtrude","SWEPT_BODY",BODY,{"disambiguationData":[OSD([sQuery(id+"F0.wireOp",EDGE,"E78.MirrorCS"),sQuery(id+"F0.wireOp",EDGE,"E79.MirrorCS"),sQuery(id+"F0.wireOp",EDGE,"E80.MirrorCS"),sQuery(id+"F0.wireOp",EDGE,"E96.MirrorCS"),sQuery(id+"F0.wireOp",EDGE,"E107.MirrorCS"),sQuery(id+"F0.wireOp",EDGE,"E108.MirrorCS"),sQuery(id+"F0.wireOp",EDGE,"E109.MirrorCS")])]});
            var Q10;
            Q10=makeQuery(id+"F9.opPattern","COPY",BODY,{"derivedFrom":makeQuery(id+"F6.opExtrude","SWEPT_BODY",BODY,{"disambiguationData":[OSD([sQuery(id+"F0.wireOp",EDGE,"E78.MirrorCS"),sQuery(id+"F0.wireOp",EDGE,"E79.MirrorCS"),sQuery(id+"F0.wireOp",EDGE,"E80.MirrorCS"),sQuery(id+"F0.wireOp",EDGE,"E96.MirrorCS"),sQuery(id+"F0.wireOp",EDGE,"E107.MirrorCS"),sQuery(id+"F0.wireOp",EDGE,"E108.MirrorCS"),sQuery(id+"F0.wireOp",EDGE,"E109.MirrorCS")])]}),"instanceName":"1"});
            transform(context, id + "F10", {"entities" : qUnion([Q0, Q1, Q2, Q3, Q4, Q5, Q6, Q7, Q8, Q9, Q10]), "transformType" : TransformType.TRANSLATION_3D, "dx" : 300 * mm, "dy" : 0 * mm, "dz" : 0 * mm, "makeCopy" : false});
        }
        {
            var Q0;
            Q0=qCreatedBy(makeId("Right.planeOp"),FACE);
            var sketch = newSketch(context, id + "F11", { "sketchPlane" : qUnion([Q0])});
            skLineSegment(sketch, "E170", {"start": v(0, 0) * mm, "end": v(-90, 0) * mm});
            skLineSegment(sketch, "E171", {"start": v(0, 0) * mm, "end": v(90, 0) * mm});
            skLineSegment(sketch, "E172", {"start": v(-90, 0) * mm, "end": v(-90, -90) * mm});
            skLineSegment(sketch, "E173", {"start": v(-90, -90) * mm, "end": v(90, -90) * mm});
            skLineSegment(sketch, "E174", {"start": v(90, -90) * mm, "end": v(90, 0) * mm});
            skLineSegment(sketch, "E175", {"start": v(0, 0) * mm, "end": v(0, -50) * mm, "construction": true});
            skCircle(sketch, "E176", {"center": v(0, -50) * mm, "radius": 11 * mm});
            skCircle(sketch, "E177", {"center": v(0, -50) * mm, "radius": 8 * mm});
            skSolve(sketch);
        }
        {
            var Q0;
            Q0=makeQuery(id+"F11.imprint","IMPRINT",FACE,{"disambiguationData":[TD([[makeQuery(id+"F11.imprint","IMPRINT",EDGE,{"derivedFrom":sQuery(id+"F11.wireOp",EDGE,"E170")}),1.0]])]});
            extrude(context, id + "F12", {"entities" : qUnion([Q0]), "oppositeDirection" : true, "depth" : 5 * mm});
        }
        {
            var Q0;
            Q0=makeQuery(id+"F12.opExtrude","SWEPT_EDGE",EDGE,{"disambiguationData":[OSD([sQuery(id+"F11.wireOp",EDGE,"E172"),sQuery(id+"F11.wireOp",EDGE,"E173")])]});
            var Q1;
            Q1=makeQuery(id+"F12.opExtrude","SWEPT_EDGE",EDGE,{"disambiguationData":[OSD([sQuery(id+"F11.wireOp",EDGE,"E173"),sQuery(id+"F11.wireOp",EDGE,"E174")])]});
            fillet(context, id + "F13", {"entities" : qUnion([Q0, Q1]), "radius" : 10 * mm, "tangentPropagation" : true, "allowEdgeOverflow" : false});
        }
        {
            var Q0;
            Q0=makeQuery(id+"F12.opExtrude","SWEPT_BODY",BODY,{"disambiguationData":[OSD([sQuery(id+"F11.wireOp",EDGE,"E170"),sQuery(id+"F11.wireOp",EDGE,"E171"),sQuery(id+"F11.wireOp",EDGE,"E172"),sQuery(id+"F11.wireOp",EDGE,"E173"),sQuery(id+"F11.wireOp",EDGE,"E174"),sQuery(id+"F11.wireOp",EDGE,"E176")])]});
            transform(context, id + "F14", {"entities" : qUnion([Q0]), "transformType" : TransformType.TRANSLATION_3D, "dx" : 1430 * mm, "dy" : 0 * mm, "dz" : 0 * mm, "makeCopy" : true});
        }
        {
            var Q0;
            Q0=makeQuery(id+"F11.imprint","IMPRINT",FACE,{"disambiguationData":[TD([[makeQuery(id+"F11.imprint","IMPRINT",EDGE,{"derivedFrom":sQuery(id+"F11.wireOp",EDGE,"E177")}),1.0]])]});
            extrude(context, id + "F15", {"entities" : qUnion([Q0]), "depth" : 1425 * mm});
        }
        {
            var Q0;
            Q0=makeQuery(id+"F12.opExtrude","CAP_FACE",FACE,{"disambiguationData":[OSD([sQuery(id+"F11.wireOp",EDGE,"E170"),sQuery(id+"F11.wireOp",EDGE,"E171"),sQuery(id+"F11.wireOp",EDGE,"E172"),sQuery(id+"F11.wireOp",EDGE,"E173"),sQuery(id+"F11.wireOp",EDGE,"E174"),sQuery(id+"F11.wireOp",EDGE,"E176")])],"isStart":false});
            var sketch = newSketch(context, id + "F16", { "sketchPlane" : qUnion([Q0])});
            skLineSegment(sketch, "E178.bottom", {"start": v(35, -85) * mm, "end": v(-35, -85) * mm});
            skLineSegment(sketch, "E178.top", {"start": v(35, -15) * mm, "end": v(-35, -15) * mm});
            skLineSegment(sketch, "E178.left", {"start": v(35, -85) * mm, "end": v(35, -15) * mm});
            skLineSegment(sketch, "E178.right", {"start": v(-35, -85) * mm, "end": v(-35, -15) * mm});
            skPoint(sketch, "E178.middle", {"position": v(0, -50) * mm});
            skSolve(sketch);
        }
        {
            var Q0;
            Q0 = qSketchRegion(id + "F16", true);
            extrude(context, id + "F17", {"entities" : qUnion([Q0]), "depth" : 135 * mm});
        }
        {
            var Q0;
            Q0=makeQuery(id+"F17.opExtrude","SWEPT_EDGE",EDGE,{"disambiguationData":[OSD([sQuery(id+"F16.wireOp",EDGE,"E178.top"),sQuery(id+"F16.wireOp",EDGE,"E178.left")])]});
            var Q1;
            Q1=makeQuery(id+"F17.opExtrude","SWEPT_EDGE",EDGE,{"disambiguationData":[OSD([sQuery(id+"F16.wireOp",EDGE,"E178.bottom"),sQuery(id+"F16.wireOp",EDGE,"E178.left")])]});
            var Q2;
            Q2=makeQuery(id+"F17.opExtrude","SWEPT_EDGE",EDGE,{"disambiguationData":[OSD([sQuery(id+"F16.wireOp",EDGE,"E178.bottom"),sQuery(id+"F16.wireOp",EDGE,"E178.right")])]});
            var Q3;
            Q3=makeQuery(id+"F17.opExtrude","SWEPT_EDGE",EDGE,{"disambiguationData":[OSD([sQuery(id+"F16.wireOp",EDGE,"E178.top"),sQuery(id+"F16.wireOp",EDGE,"E178.right")])]});
            fillet(context, id + "F18", {"entities" : qUnion([Q0, Q1, Q2, Q3]), "radius" : 10 * mm, "tangentPropagation" : true, "allowEdgeOverflow" : false});
        }
        {
            var Q0;
            Q0=makeQuery(id+"F17.opExtrude","CAP_FACE",FACE,{"disambiguationData":[OSD([sQuery(id+"F16.wireOp",EDGE,"E178.bottom"),sQuery(id+"F16.wireOp",EDGE,"E178.top"),sQuery(id+"F16.wireOp",EDGE,"E178.left"),sQuery(id+"F16.wireOp",EDGE,"E178.right")])],"isStart":false});
            var sketch = newSketch(context, id + "F19", { "sketchPlane" : qUnion([Q0])});
            skLineSegment(sketch, "E179", {"start": v(0, -85) * mm, "end": v(0, -15) * mm, "construction": true});
            skLineSegment(sketch, "E180", {"start": v(-35, -50) * mm, "end": v(35, -50) * mm, "construction": true});
            skCircle(sketch, "E181", {"center": v(0, -50) * mm, "radius": 7.5 * mm});
            skSolve(sketch);
        }
        {
            var Q0;
            Q0 = qSketchRegion(id + "F19", true);
            extrude(context, id + "F20", {"entities" : qUnion([Q0]), "depth" : 4 * mm});
        }
        {
            var Q0;
            Q0=makeQuery(id+"F20.opExtrude","CAP_FACE",FACE,{"disambiguationData":[OSD([sQuery(id+"F19.wireOp",EDGE,"E181")])],"isStart":false});
            var sketch = newSketch(context, id + "F21", { "sketchPlane" : qUnion([Q0])});
            skCircle(sketch, "E182", {"center": v(0, -50) * mm, "radius": 25 * mm});
            skSolve(sketch);
        }
        {
            var Q0;
            Q0 = qSketchRegion(id + "F21", true);
            extrude(context, id + "F22", {"entities" : qUnion([Q0]), "operationType" : NewBodyOperationType.ADD, "depth" : 14 * mm});
        }
        {
            var Q0;
            Q0=makeQuery(id+"F1.opExtrude","SWEPT_BODY",BODY,{"disambiguationData":[OSD([sQuery(id+"F0.wireOp",EDGE,"E0"),sQuery(id+"F0.wireOp",EDGE,"E1"),sQuery(id+"F0.wireOp",EDGE,"E2.MirrorCS"),sQuery(id+"F0.wireOp",EDGE,"E3.MirrorCS"),sQuery(id+"F0.wireOp",EDGE,"E5"),sQuery(id+"F0.wireOp",EDGE,"E7"),sQuery(id+"F0.wireOp",EDGE,"E8"),sQuery(id+"F0.wireOp",EDGE,"E9"),sQuery(id+"F0.wireOp",EDGE,"E10"),sQuery(id+"F0.wireOp",EDGE,"E11"),sQuery(id+"F0.wireOp",EDGE,"E13.MirrorCS"),sQuery(id+"F0.wireOp",EDGE,"E14.MirrorCS"),sQuery(id+"F0.wireOp",EDGE,"E15"),sQuery(id+"F0.wireOp",EDGE,"E16"),sQuery(id+"F0.wireOp",EDGE,"E19"),sQuery(id+"F0.wireOp",EDGE,"E20"),sQuery(id+"F0.wireOp",EDGE,"E21"),sQuery(id+"F0.wireOp",EDGE,"E22"),sQuery(id+"F0.wireOp",EDGE,"E23.MirrorCS"),sQuery(id+"F0.wireOp",EDGE,"E24.MirrorCS"),sQuery(id+"F0.wireOp",EDGE,"E25.MirrorCS"),sQuery(id+"F0.wireOp",EDGE,"E26"),sQuery(id+"F0.wireOp",EDGE,"E27.MirrorCS"),sQuery(id+"F0.wireOp",EDGE,"E29"),sQuery(id+"F0.wireOp",EDGE,"E30"),sQuery(id+"F0.wireOp",EDGE,"E31"),sQuery(id+"F0.wireOp",EDGE,"E32"),sQuery(id+"F0.wireOp",EDGE,"E33"),sQuery(id+"F0.wireOp",EDGE,"E34.MirrorCS"),sQuery(id+"F0.wireOp",EDGE,"E35.MirrorCS"),sQuery(id+"F0.wireOp",EDGE,"E36.MirrorCS"),sQuery(id+"F0.wireOp",EDGE,"E37"),sQuery(id+"F0.wireOp",EDGE,"E51.MirrorCS"),sQuery(id+"F0.wireOp",EDGE,"E52.MirrorCS"),sQuery(id+"F0.wireOp",EDGE,"E53.MirrorCS"),sQuery(id+"F0.wireOp",EDGE,"E54.MirrorCS"),sQuery(id+"F0.wireOp",EDGE,"E55.MirrorCS"),sQuery(id+"F0.wireOp",EDGE,"E56.MirrorCS"),sQuery(id+"F0.wireOp",EDGE,"E57.MirrorCS"),sQuery(id+"F0.wireOp",EDGE,"E58.MirrorCS"),sQuery(id+"F0.wireOp",EDGE,"E59.MirrorCS"),sQuery(id+"F0.wireOp",EDGE,"E60.MirrorCS"),sQuery(id+"F0.wireOp",EDGE,"E61.MirrorCS"),sQuery(id+"F0.wireOp",EDGE,"E62.MirrorCS"),sQuery(id+"F0.wireOp",EDGE,"E63.MirrorCS"),sQuery(id+"F0.wireOp",EDGE,"E64.MirrorCS"),sQuery(id+"F0.wireOp",EDGE,"E65.MirrorCS"),sQuery(id+"F0.wireOp",EDGE,"E66.MirrorCS"),sQuery(id+"F0.wireOp",EDGE,"E67.MirrorCS"),sQuery(id+"F0.wireOp",EDGE,"E68.MirrorCS"),sQuery(id+"F0.wireOp",EDGE,"E69.MirrorCS"),sQuery(id+"F0.wireOp",EDGE,"E70.MirrorCS"),sQuery(id+"F0.wireOp",EDGE,"E71.MirrorCS"),sQuery(id+"F0.wireOp",EDGE,"E72.MirrorCS"),sQuery(id+"F0.wireOp",EDGE,"E73.MirrorCS"),sQuery(id+"F0.wireOp",EDGE,"E74.MirrorCS")])]});
            var Q1;
            Q1=makeQuery(id+"F2.opExtrude","SWEPT_BODY",BODY,{"disambiguationData":[OSD([sQuery(id+"F0.wireOp",EDGE,"E26"),sQuery(id+"F0.wireOp",EDGE,"E40"),sQuery(id+"F0.wireOp",EDGE,"E43"),sQuery(id+"F0.wireOp",EDGE,"E45"),sQuery(id+"F0.wireOp",EDGE,"E46"),sQuery(id+"F0.wireOp",EDGE,"E48.MirrorCS"),sQuery(id+"F0.wireOp",EDGE,"E49.MirrorCS"),sQuery(id+"F0.wireOp",EDGE,"E50.MirrorCS")])]});
            var Q2;
            Q2=makeQuery(id+"F2.opExtrude","SWEPT_BODY",BODY,{"disambiguationData":[OSD([sQuery(id+"F0.wireOp",EDGE,"E27.MirrorCS"),sQuery(id+"F0.wireOp",EDGE,"E75.MirrorCS"),sQuery(id+"F0.wireOp",EDGE,"E76.MirrorCS"),sQuery(id+"F0.wireOp",EDGE,"E77.MirrorCS"),sQuery(id+"F0.wireOp",EDGE,"E78.MirrorCS"),sQuery(id+"F0.wireOp",EDGE,"E79.MirrorCS"),sQuery(id+"F0.wireOp",EDGE,"E80.MirrorCS"),sQuery(id+"F0.wireOp",EDGE,"E81")])]});
            var Q3;
            Q3=makeQuery(id+"F4.opExtrude","SWEPT_BODY",BODY,{"disambiguationData":[OSD([sQuery(id+"F0.wireOp",EDGE,"E85"),sQuery(id+"F0.wireOp",EDGE,"E88"),sQuery(id+"F0.wireOp",EDGE,"E95"),sQuery(id+"F0.wireOp",EDGE,"E98")])]});
            var Q4;
            Q4=makeQuery(id+"F4.opExtrude","SWEPT_BODY",BODY,{"disambiguationData":[OSD([sQuery(id+"F0.wireOp",EDGE,"E92.MirrorCS"),sQuery(id+"F0.wireOp",EDGE,"E94.MirrorCS"),sQuery(id+"F0.wireOp",EDGE,"E96.MirrorCS"),sQuery(id+"F0.wireOp",EDGE,"E97")])]});
            var Q5;
            Q5=makeQuery(id+"F5.opExtrude","SWEPT_BODY",BODY,{"disambiguationData":[OSD([sQuery(id+"F0.wireOp",EDGE,"E84"),sQuery(id+"F0.wireOp",EDGE,"E85"),sQuery(id+"F0.wireOp",EDGE,"E89"),sQuery(id+"F0.wireOp",EDGE,"E92.MirrorCS"),sQuery(id+"F0.wireOp",EDGE,"E93.MirrorCS"),sQuery(id+"F0.wireOp",EDGE,"E97"),sQuery(id+"F0.wireOp",EDGE,"E98"),sQuery(id+"F0.wireOp",EDGE,"E113"),sQuery(id+"F0.wireOp",EDGE,"E115"),sQuery(id+"F0.wireOp",EDGE,"E117"),sQuery(id+"F0.wireOp",EDGE,"E118"),sQuery(id+"F0.wireOp",EDGE,"E120"),sQuery(id+"F0.wireOp",EDGE,"E121"),sQuery(id+"F0.wireOp",EDGE,"E122"),sQuery(id+"F0.wireOp",EDGE,"E123"),sQuery(id+"F0.wireOp",EDGE,"E124.MirrorCS"),sQuery(id+"F0.wireOp",EDGE,"E125.MirrorCS"),sQuery(id+"F0.wireOp",EDGE,"E126.MirrorCS"),sQuery(id+"F0.wireOp",EDGE,"E128.MirrorCS"),sQuery(id+"F0.wireOp",EDGE,"E129.MirrorCS"),sQuery(id+"F0.wireOp",EDGE,"E130.MirrorCS"),sQuery(id+"F0.wireOp",EDGE,"E131.MirrorCS"),sQuery(id+"F0.wireOp",EDGE,"E132.MirrorCS"),sQuery(id+"F0.wireOp",EDGE,"E133.MirrorCS"),sQuery(id+"F0.wireOp",EDGE,"E134.MirrorCS"),sQuery(id+"F0.wireOp",EDGE,"E135.MirrorCS"),sQuery(id+"F0.wireOp",EDGE,"E136.MirrorCS"),sQuery(id+"F0.wireOp",EDGE,"E137.MirrorCS"),sQuery(id+"F0.wireOp",EDGE,"E138.MirrorCS"),sQuery(id+"F0.wireOp",EDGE,"E139.MirrorCS"),sQuery(id+"F0.wireOp",EDGE,"E140.MirrorCS"),sQuery(id+"F0.wireOp",EDGE,"E141.MirrorCS"),sQuery(id+"F0.wireOp",EDGE,"E142.MirrorCS"),sQuery(id+"F0.wireOp",EDGE,"E143.MirrorCS"),sQuery(id+"F0.wireOp",EDGE,"E144.MirrorCS"),sQuery(id+"F0.wireOp",EDGE,"E145.MirrorCS"),sQuery(id+"F0.wireOp",EDGE,"E146.MirrorCS"),sQuery(id+"F0.wireOp",EDGE,"E147.MirrorCS"),sQuery(id+"F0.wireOp",EDGE,"E148.MirrorCS"),sQuery(id+"F0.wireOp",EDGE,"E149.MirrorCS"),sQuery(id+"F0.wireOp",EDGE,"E150.MirrorCS"),sQuery(id+"F0.wireOp",EDGE,"E151.MirrorCS"),sQuery(id+"F0.wireOp",EDGE,"E154"),sQuery(id+"F0.wireOp",EDGE,"E155"),sQuery(id+"F0.wireOp",EDGE,"E156"),sQuery(id+"F0.wireOp",EDGE,"E158.MirrorCS"),sQuery(id+"F0.wireOp",EDGE,"E159.MirrorCS"),sQuery(id+"F0.wireOp",EDGE,"E160.MirrorCS"),sQuery(id+"F0.wireOp",EDGE,"E161.MirrorCS"),sQuery(id+"F0.wireOp",EDGE,"E163.MirrorCS"),sQuery(id+"F0.wireOp",EDGE,"E164.MirrorCS"),sQuery(id+"F0.wireOp",EDGE,"E165.MirrorCS"),sQuery(id+"F0.wireOp",EDGE,"E166.MirrorCS"),sQuery(id+"F0.wireOp",EDGE,"E167.MirrorCS"),sQuery(id+"F0.wireOp",EDGE,"E168.MirrorCS"),sQuery(id+"F0.wireOp",EDGE,"E169.MirrorCS")])]});
            var Q6;
            Q6=makeQuery(id+"F6.opExtrude","SWEPT_BODY",BODY,{"disambiguationData":[OSD([sQuery(id+"F0.wireOp",EDGE,"E40"),sQuery(id+"F0.wireOp",EDGE,"E43"),sQuery(id+"F0.wireOp",EDGE,"E45"),sQuery(id+"F0.wireOp",EDGE,"E95"),sQuery(id+"F0.wireOp",EDGE,"E103.MirrorCS"),sQuery(id+"F0.wireOp",EDGE,"E104.MirrorCS"),sQuery(id+"F0.wireOp",EDGE,"E105.MirrorCS")])]});
            var Q7;
            Q7=makeQuery(id+"F6.opExtrude","SWEPT_BODY",BODY,{"disambiguationData":[OSD([sQuery(id+"F0.wireOp",EDGE,"E48.MirrorCS"),sQuery(id+"F0.wireOp",EDGE,"E49.MirrorCS"),sQuery(id+"F0.wireOp",EDGE,"E50.MirrorCS"),sQuery(id+"F0.wireOp",EDGE,"E95"),sQuery(id+"F0.wireOp",EDGE,"E110.MirrorCS"),sQuery(id+"F0.wireOp",EDGE,"E111.MirrorCS"),sQuery(id+"F0.wireOp",EDGE,"E112.MirrorCS")])]});
            var Q8;
            Q8=makeQuery(id+"F6.opExtrude","SWEPT_BODY",BODY,{"disambiguationData":[OSD([sQuery(id+"F0.wireOp",EDGE,"E75.MirrorCS"),sQuery(id+"F0.wireOp",EDGE,"E76.MirrorCS"),sQuery(id+"F0.wireOp",EDGE,"E77.MirrorCS"),sQuery(id+"F0.wireOp",EDGE,"E96.MirrorCS"),sQuery(id+"F0.wireOp",EDGE,"E100"),sQuery(id+"F0.wireOp",EDGE,"E101"),sQuery(id+"F0.wireOp",EDGE,"E102")])]});
            var Q9;
            Q9=makeQuery(id+"F6.opExtrude","SWEPT_BODY",BODY,{"disambiguationData":[OSD([sQuery(id+"F0.wireOp",EDGE,"E78.MirrorCS"),sQuery(id+"F0.wireOp",EDGE,"E79.MirrorCS"),sQuery(id+"F0.wireOp",EDGE,"E80.MirrorCS"),sQuery(id+"F0.wireOp",EDGE,"E96.MirrorCS"),sQuery(id+"F0.wireOp",EDGE,"E107.MirrorCS"),sQuery(id+"F0.wireOp",EDGE,"E108.MirrorCS"),sQuery(id+"F0.wireOp",EDGE,"E109.MirrorCS")])]});
            var Q10;
            Q10=makeQuery(id+"F9.opPattern","COPY",BODY,{"derivedFrom":makeQuery(id+"F6.opExtrude","SWEPT_BODY",BODY,{"disambiguationData":[OSD([sQuery(id+"F0.wireOp",EDGE,"E40"),sQuery(id+"F0.wireOp",EDGE,"E43"),sQuery(id+"F0.wireOp",EDGE,"E45"),sQuery(id+"F0.wireOp",EDGE,"E95"),sQuery(id+"F0.wireOp",EDGE,"E103.MirrorCS"),sQuery(id+"F0.wireOp",EDGE,"E104.MirrorCS"),sQuery(id+"F0.wireOp",EDGE,"E105.MirrorCS")])]}),"instanceName":"1"});
            var Q11;
            Q11=makeQuery(id+"F9.opPattern","COPY",BODY,{"derivedFrom":makeQuery(id+"F6.opExtrude","SWEPT_BODY",BODY,{"disambiguationData":[OSD([sQuery(id+"F0.wireOp",EDGE,"E48.MirrorCS"),sQuery(id+"F0.wireOp",EDGE,"E49.MirrorCS"),sQuery(id+"F0.wireOp",EDGE,"E50.MirrorCS"),sQuery(id+"F0.wireOp",EDGE,"E95"),sQuery(id+"F0.wireOp",EDGE,"E110.MirrorCS"),sQuery(id+"F0.wireOp",EDGE,"E111.MirrorCS"),sQuery(id+"F0.wireOp",EDGE,"E112.MirrorCS")])]}),"instanceName":"1"});
            var Q12;
            Q12=makeQuery(id+"F9.opPattern","COPY",BODY,{"derivedFrom":makeQuery(id+"F6.opExtrude","SWEPT_BODY",BODY,{"disambiguationData":[OSD([sQuery(id+"F0.wireOp",EDGE,"E75.MirrorCS"),sQuery(id+"F0.wireOp",EDGE,"E76.MirrorCS"),sQuery(id+"F0.wireOp",EDGE,"E77.MirrorCS"),sQuery(id+"F0.wireOp",EDGE,"E96.MirrorCS"),sQuery(id+"F0.wireOp",EDGE,"E100"),sQuery(id+"F0.wireOp",EDGE,"E101"),sQuery(id+"F0.wireOp",EDGE,"E102")])]}),"instanceName":"1"});
            var Q13;
            Q13=makeQuery(id+"F9.opPattern","COPY",BODY,{"derivedFrom":makeQuery(id+"F6.opExtrude","SWEPT_BODY",BODY,{"disambiguationData":[OSD([sQuery(id+"F0.wireOp",EDGE,"E78.MirrorCS"),sQuery(id+"F0.wireOp",EDGE,"E79.MirrorCS"),sQuery(id+"F0.wireOp",EDGE,"E80.MirrorCS"),sQuery(id+"F0.wireOp",EDGE,"E96.MirrorCS"),sQuery(id+"F0.wireOp",EDGE,"E107.MirrorCS"),sQuery(id+"F0.wireOp",EDGE,"E108.MirrorCS"),sQuery(id+"F0.wireOp",EDGE,"E109.MirrorCS")])]}),"instanceName":"1"});
            var Q14;
            Q14=makeQuery(id+"F12.opExtrude","SWEPT_BODY",BODY,{"disambiguationData":[OSD([sQuery(id+"F11.wireOp",EDGE,"E170"),sQuery(id+"F11.wireOp",EDGE,"E171"),sQuery(id+"F11.wireOp",EDGE,"E172"),sQuery(id+"F11.wireOp",EDGE,"E173"),sQuery(id+"F11.wireOp",EDGE,"E174"),sQuery(id+"F11.wireOp",EDGE,"E176")])]});
            var Q15;
            Q15=makeQuery(id+"F14.opPattern","COPY",BODY,{"derivedFrom":makeQuery(id+"F12.opExtrude","SWEPT_BODY",BODY,{"disambiguationData":[OSD([sQuery(id+"F11.wireOp",EDGE,"E170"),sQuery(id+"F11.wireOp",EDGE,"E171"),sQuery(id+"F11.wireOp",EDGE,"E172"),sQuery(id+"F11.wireOp",EDGE,"E173"),sQuery(id+"F11.wireOp",EDGE,"E174"),sQuery(id+"F11.wireOp",EDGE,"E176")])]}),"instanceName":"1"});
            var Q16;
            Q16=makeQuery(id+"F15.opExtrude","SWEPT_BODY",BODY,{"disambiguationData":[OSD([sQuery(id+"F11.wireOp",EDGE,"E177")])]});
            var Q17;
            Q17=makeQuery(id+"F17.opExtrude","SWEPT_BODY",BODY,{"disambiguationData":[OSD([sQuery(id+"F16.wireOp",EDGE,"E178.bottom"),sQuery(id+"F16.wireOp",EDGE,"E178.top"),sQuery(id+"F16.wireOp",EDGE,"E178.left"),sQuery(id+"F16.wireOp",EDGE,"E178.right")])]});
            var Q18;
            Q18=makeQuery(id+"F20.opExtrude","SWEPT_BODY",BODY,{"disambiguationData":[OSD([sQuery(id+"F19.wireOp",EDGE,"E181")])]});
            transform(context, id + "F23", {"entities" : qUnion([Q0, Q1, Q2, Q3, Q4, Q5, Q6, Q7, Q8, Q9, Q10, Q11, Q12, Q13, Q14, Q15, Q16, Q17, Q18]), "transformType" : TransformType.TRANSLATION_3D, "dx" : -10 * mm, "dy" : 450 * mm, "dz" : 740 * mm, "makeCopy" : false});
        }
    });
